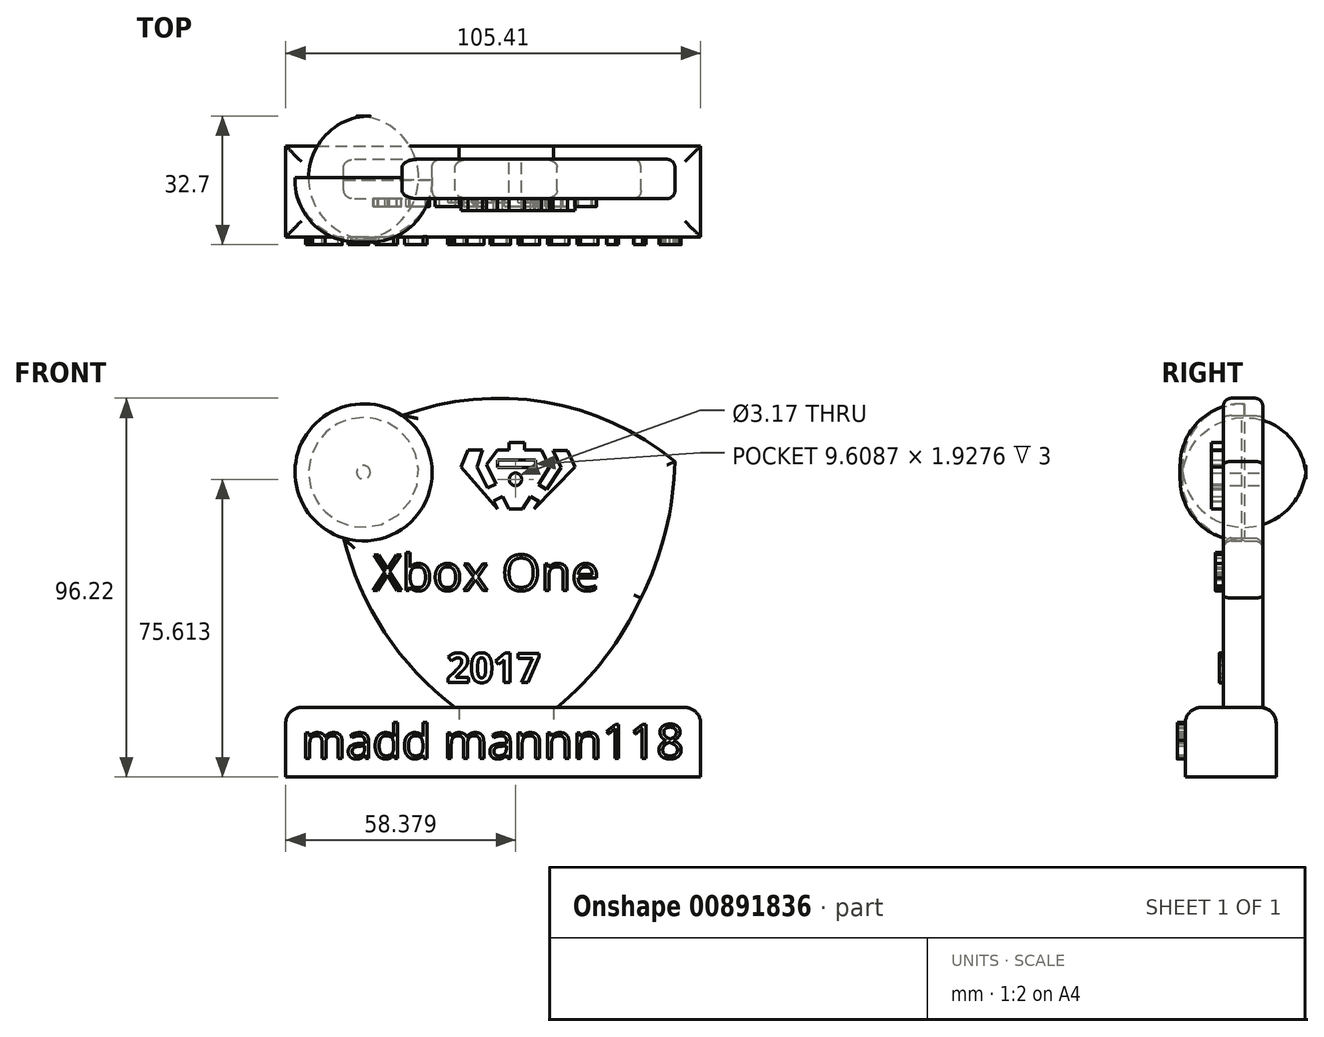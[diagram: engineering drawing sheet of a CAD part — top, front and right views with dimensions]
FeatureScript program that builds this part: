
annotation { "Feature Type Name" : "Feature", "Feature Type Description" : "" }
export const myFeature = defineFeature(function(context is Context, id is Id, definition is map)
    precondition{}
    {
        {
            var Q0;
            Q0=qCreatedBy(makeId("Front.planeOp"),FACE);
            var sketch = newSketch(context, id + "F0", { "sketchPlane" : qUnion([Q0])});
            skArc(sketch, "E0", {"start": v(0, -36.03) * mm, "mid": v(19.7, -20.75) * mm, "end": v(33.53, 0) * mm});
            skArc(sketch, "E1", {"start": v(33.53, 0) * mm, "mid": v(39.77, 16.9) * mm, "end": v(42.15, 34.74) * mm});
            skCircle(sketch, "E2", {"center": v(-36.94, 31.97) * mm, "radius": 17.42 * mm});
            skArc(sketch, "E3", {"start": v(-42.01, 15.3) * mm, "mid": v(-26.81, -15.11) * mm, "end": v(0, -36.03) * mm});
            skPoint(sketch, "E4.end.orphan", {"position": v(0, 41.46) * mm});
            skArc(sketch, "E5", {"start": v(42.15, 34.74) * mm, "mid": v(0.72, 50.74) * mm, "end": v(-42.01, 38.66) * mm});
            skSolve(sketch);
        }
        {
            var Q0;
            {var subQ0=sQuery(id+"F0.wireOp",EDGE,"E2");var subQ1=makeQuery(id+"F0.imprint","INTERSECT",VERTEX,{"derivedFrom":[subQ0,sQuery(id+"F0.wireOp",EDGE,"E3")]});Q0=makeQuery(id+"F0.imprint","IMPRINT",FACE,{"disambiguationData":[TD([[makeQuery(id+"F0.imprint","IMPRINT",EDGE,{"disambiguationData":[TD([[subQ1,1.0]])],"derivedFrom":subQ0}),1.0]])]});}
            extrude(context, id + "F1", {"entities" : qUnion([Q0]), "depth" : 16 * mm, "offsetDistance" : 25 * mm, "hasSecondDirection" : true, "secondDirectionOppositeDirection" : true, "secondDirectionDepth" : 16 * mm});
        }
        {
            var Q0;
            Q0=makeQuery(id+"F1.opExtrude","CAP_EDGE",EDGE,{"disambiguationData":[OSD([sQuery(id+"F0.wireOp",EDGE,"E2")])],"isStart":false});
            var Q1;
            Q1=makeQuery(id+"F1.opExtrude","CAP_EDGE",EDGE,{"disambiguationData":[OSD([sQuery(id+"F0.wireOp",EDGE,"E2")])],"isStart":true});
            fillet(context, id + "F2", {"entities" : qUnion([Q0, Q1]), "radius" : 15.7 * mm, "tangentPropagation" : true, "allowEdgeOverflow" : false});
        }
        {
            var Q0;
            Q0=makeQuery(id+"F0.imprint","IMPRINT",FACE,{"disambiguationData":[TD([[makeQuery(id+"F0.imprint","IMPRINT",EDGE,{"derivedFrom":sQuery(id+"F0.wireOp",EDGE,"E0")}),1.0]])]});
            extrude(context, id + "F3", {"entities" : qUnion([Q0]), "operationType" : NewBodyOperationType.ADD, "depth" : 5 * mm, "offsetDistance" : 25 * mm, "hasSecondDirection" : true, "secondDirectionOppositeDirection" : true, "secondDirectionDepth" : 5 * mm});
        }
        {
            var Q0;
            Q0=makeQuery(id+"F3.opExtrude","CAP_FACE",FACE,{"disambiguationData":[OSD([sQuery(id+"F0.wireOp",EDGE,"E0"),sQuery(id+"F0.wireOp",EDGE,"E1"),sQuery(id+"F0.wireOp",EDGE,"E2"),sQuery(id+"F0.wireOp",EDGE,"E3"),sQuery(id+"F0.wireOp",EDGE,"E5")])],"isStart":false});
            cPlane(context, id + "F4", {"entities" : qUnion([Q0]), "cplaneType" : CPlaneType.OFFSET, "offset" : 0 * mm, "width" : 150 * mm, "height" : 150 * mm});
        }
        {
            var Q0;
            Q0=qCreatedBy(id+"F4.planeOp",FACE);
            var sketch = newSketch(context, id + "F5", { "sketchPlane" : qUnion([Q0])});
            skText(sketch, "E6", { "text": "Rocket league\n", "fontName": "OpenSans-Regular.ttf"});
            const initialGuessF5  = {"E6": [-0.03247, -0.00599, 1, 0, 0.0069]};
            skSetInitialGuess(sketch, initialGuessF5);
            skSolve(sketch);
        }
        {
            var Q0;
            Q0 = qConstructionFilter(qBodyType(qCreatedBy(id + "F5" ,EDGE), BodyType.WIRE), ConstructionObject.NO);
            extrude(context, id + "F6", {"bodyType" : ToolBodyType.SURFACE, "surfaceEntities" : qUnion([Q0]), "depth" : 1 * mm, "offsetDistance" : 25 * mm, "hasSecondDirection" : true, "secondDirectionOppositeDirection" : true, "secondDirectionDepth" : 3 * mm});
        }
        {
            var Q0;
            Q0=makeQuery(id+"F3.opExtrude","CAP_EDGE",EDGE,{"disambiguationData":[OSD([sQuery(id+"F0.wireOp",EDGE,"E2")])],"isStart":false});
            var Q1;
            Q1=makeQuery(id+"F3.opExtrude","CAP_EDGE",EDGE,{"disambiguationData":[OSD([sQuery(id+"F0.wireOp",EDGE,"E3")])],"isStart":false});
            var Q2;
            Q2=makeQuery(id+"F3.opExtrude","CAP_EDGE",EDGE,{"disambiguationData":[OSD([sQuery(id+"F0.wireOp",EDGE,"E0")])],"isStart":false});
            var Q3;
            Q3=makeQuery(id+"F3.opExtrude","CAP_EDGE",EDGE,{"disambiguationData":[OSD([sQuery(id+"F0.wireOp",EDGE,"E1")])],"isStart":false});
            var Q4;
            Q4=makeQuery(id+"F3.opExtrude","CAP_EDGE",EDGE,{"disambiguationData":[OSD([sQuery(id+"F0.wireOp",EDGE,"E5")])],"isStart":false});
            var Q5;
            Q5=makeQuery(id+"F3.opExtrude","CAP_EDGE",EDGE,{"disambiguationData":[OSD([sQuery(id+"F0.wireOp",EDGE,"E2")])],"isStart":true});
            var Q6;
            Q6=makeQuery(id+"F3.opExtrude","CAP_EDGE",EDGE,{"disambiguationData":[OSD([sQuery(id+"F0.wireOp",EDGE,"E3")])],"isStart":true});
            var Q7;
            Q7=makeQuery(id+"F3.opExtrude","CAP_EDGE",EDGE,{"disambiguationData":[OSD([sQuery(id+"F0.wireOp",EDGE,"E0")])],"isStart":true});
            var Q8;
            Q8=makeQuery(id+"F3.opExtrude","CAP_EDGE",EDGE,{"disambiguationData":[OSD([sQuery(id+"F0.wireOp",EDGE,"E1")])],"isStart":true});
            var Q9;
            Q9=makeQuery(id+"F3.opExtrude","CAP_EDGE",EDGE,{"disambiguationData":[OSD([sQuery(id+"F0.wireOp",EDGE,"E5")])],"isStart":true});
            fillet(context, id + "F7", {"entities" : qUnion([Q0, Q1, Q2, Q3, Q4, Q5, Q6, Q7, Q8, Q9]), "radius" : 2 * mm, "tangentPropagation" : true, "allowEdgeOverflow" : false});
        }
        {
            var Q0;
            Q0=qCreatedBy(id+"F4.planeOp",FACE);
            var sketch = newSketch(context, id + "F8", { "sketchPlane" : qUnion([Q0])});
            skLineSegment(sketch, "E7", {"start": v(-2.84, 22.63) * mm, "end": v(-8.12, 33.39) * mm});
            skLineSegment(sketch, "E8", {"start": v(-8.12, 33.39) * mm, "end": v(-6.7, 37.65) * mm});
            skLineSegment(sketch, "E9", {"start": v(-6.7, 37.65) * mm, "end": v(-10.35, 37.65) * mm});
            skLineSegment(sketch, "E10", {"start": v(-10.35, 37.65) * mm, "end": v(-12.18, 33.39) * mm});
            skLineSegment(sketch, "E11", {"start": v(-12.18, 33.39) * mm, "end": v(-2.84, 22.63) * mm});
            skLineSegment(sketch, "E12", {"start": v(0, 22.63) * mm, "end": v(3.45, 22.63) * mm});
            skLineSegment(sketch, "E13", {"start": v(3.45, 22.63) * mm, "end": v(5.48, 25.88) * mm});
            skLineSegment(sketch, "E14", {"start": v(7.49, 28.86) * mm, "end": v(10.32, 33.39) * mm});
            skLineSegment(sketch, "E15", {"start": v(10.32, 33.39) * mm, "end": v(8.23, 37.65) * mm});
            skLineSegment(sketch, "E16", {"start": v(8.23, 37.65) * mm, "end": v(-2.84, 37.65) * mm});
            skLineSegment(sketch, "E17", {"start": v(0, 22.63) * mm, "end": v(-1.6, 25.88) * mm});
            skLineSegment(sketch, "E18", {"start": v(-1.6, 25.88) * mm, "end": v(-3.88, 24.75) * mm});
            skLineSegment(sketch, "E19", {"start": v(-3.88, 24.75) * mm, "end": v(-5.48, 28) * mm});
            skLineSegment(sketch, "E20", {"start": v(-5.48, 28) * mm, "end": v(-3.32, 29.07) * mm});
            skLineSegment(sketch, "E21", {"start": v(-3.32, 29.07) * mm, "end": v(-5.73, 33.97) * mm});
            skLineSegment(sketch, "E22", {"start": v(-5.73, 33.97) * mm, "end": v(-2.84, 37.65) * mm});
            skLineSegment(sketch, "E23", {"start": v(6.33, 22.63) * mm, "end": v(13.22, 33.24) * mm});
            skLineSegment(sketch, "E24", {"start": v(13.22, 33.24) * mm, "end": v(11.15, 37.48) * mm});
            skLineSegment(sketch, "E25", {"start": v(11.15, 37.48) * mm, "end": v(14.84, 37.48) * mm});
            skLineSegment(sketch, "E26", {"start": v(14.84, 37.48) * mm, "end": v(16.85, 33.39) * mm});
            skLineSegment(sketch, "E27", {"start": v(16.85, 33.39) * mm, "end": v(6.33, 22.63) * mm});
            skLineSegment(sketch, "E28", {"start": v(5.48, 25.88) * mm, "end": v(7.98, 24.32) * mm});
            skLineSegment(sketch, "E29", {"start": v(7.49, 28.86) * mm, "end": v(10.55, 26.95) * mm});
            skLineSegment(sketch, "E30", {"start": v(-1.6, 25.88) * mm, "end": v(1.79, 27.54) * mm});
            skLineSegment(sketch, "E31", {"start": v(1.79, 27.54) * mm, "end": v(5.48, 25.88) * mm});
            skLineSegment(sketch, "E32", {"start": v(-3.32, 29.07) * mm, "end": v(0, 30.7) * mm});
            skLineSegment(sketch, "E33", {"start": v(0, 30.7) * mm, "end": v(1.79, 27.54) * mm});
            skLineSegment(sketch, "E34", {"start": v(7.49, 28.86) * mm, "end": v(4, 31.12) * mm});
            skPoint(sketch, "E34.endSnap0", {"position": v(8.9, 31.12) * mm});
            skLineSegment(sketch, "E35", {"start": v(4, 31.12) * mm, "end": v(1.79, 27.54) * mm});
            skLineSegment(sketch, "E36", {"start": v(4, 31.12) * mm, "end": v(4, 39.53) * mm});
            skLineSegment(sketch, "E37", {"start": v(4, 39.53) * mm, "end": v(0, 39.53) * mm});
            skLineSegment(sketch, "E38", {"start": v(0, 39.53) * mm, "end": v(0, 30.7) * mm});
            skLineSegment(sketch, "E39", {"start": v(0, 30.7) * mm, "end": v(4, 31.12) * mm});
            skLineSegment(sketch, "E40", {"start": v(-2.84, 35.11) * mm, "end": v(6.77, 35.11) * mm});
            skPoint(sketch, "E40.startSnap0", {"position": v(0, 35.11) * mm});
            skLineSegment(sketch, "E41", {"start": v(6.77, 35.11) * mm, "end": v(6.77, 33.18) * mm});
            skLineSegment(sketch, "E42", {"start": v(6.77, 33.18) * mm, "end": v(-2.84, 33.18) * mm});
            skLineSegment(sketch, "E43", {"start": v(-2.84, 33.18) * mm, "end": v(-2.84, 35.11) * mm});
            skSolve(sketch);
        }
        {
            var Q0;
            {var subQ0=sQuery(id+"F8.wireOp",EDGE,"E38");var subQ1=sQuery(id+"F8.wireOp",EDGE,"E16");var subQ2=makeQuery(id+"F8.imprint","INTERSECT",VERTEX,{"derivedFrom":[subQ1,subQ0]});var subQ5=makeQuery(id+"F8.imprint","IMPRINT",EDGE,{"disambiguationData":[TD([[subQ2,1.0]])],"derivedFrom":subQ1});var subQ6=sQuery(id+"F8.wireOp",EDGE,"E37");var subQ12=sQuery(id+"F8.wireOp",EDGE,"E29");var subQ13=sQuery(id+"F8.wireOp",EDGE,"E23");var subQ14=makeQuery(id+"F8.imprint","INTERSECT",VERTEX,{"derivedFrom":[subQ13,subQ12]});var subQ15=sQuery(id+"F8.wireOp",EDGE,"E28");var subQ16=makeQuery(id+"F8.imprint","INTERSECT",VERTEX,{"derivedFrom":[subQ13,subQ15]});var subQ17=makeQuery(id+"F8.imprint","IMPRINT",EDGE,{"disambiguationData":[TD([[subQ14,1.0]])],"derivedFrom":subQ13});var subQ23=sQuery(id+"F8.wireOp",EDGE,"E31");var subQ24=makeQuery(id+"F8.imprint","IMPRINT",EDGE,{"derivedFrom":subQ23});var subQ27=sQuery(id+"F8.wireOp",EDGE,"E14");var subQ31=sQuery(id+"F8.wireOp",EDGE,"E8");var subQ32=sQuery(id+"F8.wireOp",EDGE,"E18");var subQ48=sQuery(id+"F8.wireOp",EDGE,"E24");Q0=qUnion([makeQuery(id+"F8.imprint","IMPRINT",FACE,{"disambiguationData":[TD([[makeQuery(id+"F8.imprint","IMPRINT",EDGE,{"derivedFrom":sQuery(id+"F8.wireOp",EDGE,"E21")}),-1.0]])]}),makeQuery(id+"F8.imprint","IMPRINT",FACE,{"disambiguationData":[TD([[makeQuery(id+"F8.imprint","IMPRINT",EDGE,{"derivedFrom":subQ48}),-1.0]])]}),makeQuery(id+"F8.imprint","IMPRINT",FACE,{"disambiguationData":[TD([[makeQuery(id+"F8.imprint","IMPRINT",EDGE,{"derivedFrom":subQ32}),-1.0]])]}),makeQuery(id+"F8.imprint","IMPRINT",FACE,{"disambiguationData":[TD([[makeQuery(id+"F8.imprint","IMPRINT",EDGE,{"disambiguationData":[TD([[subQ16,1.0]])],"derivedFrom":subQ13}),-1.0]])]}),makeQuery(id+"F8.imprint","IMPRINT",FACE,{"disambiguationData":[TD([[makeQuery(id+"F8.imprint","IMPRINT",EDGE,{"derivedFrom":subQ27}),1.0]])]}),makeQuery(id+"F8.imprint","IMPRINT",FACE,{"disambiguationData":[TD([[makeQuery(id+"F8.imprint","IMPRINT",EDGE,{"derivedFrom":subQ31}),1.0]])]}),makeQuery(id+"F8.imprint","IMPRINT",FACE,{"disambiguationData":[TD([[makeQuery(id+"F8.imprint","IMPRINT",EDGE,{"derivedFrom":sQuery(id+"F8.wireOp",EDGE,"E12")}),1.0]])]}),makeQuery(id+"F8.imprint","IMPRINT",FACE,{"disambiguationData":[TD([[subQ24,1.0]])]}),makeQuery(id+"F8.imprint","IMPRINT",FACE,{"disambiguationData":[TD([[subQ17,-1.0]])]}),makeQuery(id+"F8.imprint","IMPRINT",FACE,{"disambiguationData":[TD([[subQ5,1.0]])]}),makeQuery(id+"F8.imprint","IMPRINT",FACE,{"disambiguationData":[TD([[makeQuery(id+"F8.imprint","IMPRINT",EDGE,{"derivedFrom":subQ6}),1.0]])]})]);}
            var Q1;
            Q1=makeQuery(id+"F8.imprint","IMPRINT",FACE,{"disambiguationData":[TD([[makeQuery(id+"F8.imprint","IMPRINT",EDGE,{"derivedFrom":sQuery(id+"F8.wireOp",EDGE,"E33")}),1.0]])]});
            var Q2;
            {var subQ0=sQuery(id+"F8.wireOp",EDGE,"E39");Q2=makeQuery(id+"F8.imprint","IMPRINT",FACE,{"disambiguationData":[TD([[makeQuery(id+"F8.imprint","IMPRINT",EDGE,{"derivedFrom":subQ0}),1.0]])]});}
            extrude(context, id + "F9", {"entities" : qUnion([Q0, Q1, Q2]), "operationType" : NewBodyOperationType.ADD, "depth" : 3 * mm, "offsetDistance" : 25 * mm});
        }
        {
            var Q0;
            Q0=qCreatedBy(id+"F4.planeOp",FACE);
            var sketch = newSketch(context, id + "F10", { "sketchPlane" : qUnion([Q0])});
            skCircle(sketch, "E44", {"center": v(1.67, 30.2) * mm, "radius": 1.58 * mm});
            skSolve(sketch);
        }
        {
            var Q0;
            Q0 = qSketchRegion(id + "F10", true);
            extrude(context, id + "F11", {"entities" : qUnion([Q0]), "operationType" : NewBodyOperationType.REMOVE, "depth" : 47.6 * mm, "offsetDistance" : 25 * mm, "hasSecondDirection" : true, "secondDirectionOppositeDirection" : true, "secondDirectionDepth" : 25 * mm});
        }
        {
            var Q0;
            Q0=qCreatedBy(makeId("Front.planeOp"),FACE);
            var sketch = newSketch(context, id + "F12", { "sketchPlane" : qUnion([Q0])});
            skLineSegment(sketch, "E45.bottom", {"start": v(-56.7, -45.4) * mm, "end": v(48.7, -45.4) * mm});
            skLineSegment(sketch, "E45.top", {"start": v(-56.7, -27.77) * mm, "end": v(48.7, -27.77) * mm});
            skLineSegment(sketch, "E45.left", {"start": v(-56.7, -45.4) * mm, "end": v(-56.7, -27.77) * mm});
            skLineSegment(sketch, "E45.right", {"start": v(48.7, -45.4) * mm, "end": v(48.7, -27.77) * mm});
            skSolve(sketch);
        }
        {
            var Q0;
            Q0 = qSketchRegion(id + "F12", true);
            extrude(context, id + "F13", {"entities" : qUnion([Q0]), "operationType" : NewBodyOperationType.ADD, "depth" : 14.7 * mm, "offsetDistance" : 25 * mm, "hasSecondDirection" : true, "secondDirectionOppositeDirection" : true, "secondDirectionDepth" : 8.4 * mm});
        }
        {
            var Q0;
            Q0=makeQuery(id+"F13.opExtrude","CAP_FACE",FACE,{"disambiguationData":[OSD([sQuery(id+"F12.wireOp",EDGE,"E45.bottom"),sQuery(id+"F12.wireOp",EDGE,"E45.top"),sQuery(id+"F12.wireOp",EDGE,"E45.left"),sQuery(id+"F12.wireOp",EDGE,"E45.right")])],"isStart":false});
            cPlane(context, id + "F14", {"entities" : qUnion([Q0]), "cplaneType" : CPlaneType.OFFSET, "offset" : 0 * mm, "width" : 150 * mm, "height" : 150 * mm});
        }
        {
            var Q0;
            Q0=qCreatedBy(id+"F14.planeOp",FACE);
            var sketch = newSketch(context, id + "F15", { "sketchPlane" : qUnion([Q0])});
            skText(sketch, "E46", { "text": "madd mannn118\n", "fontName": "OpenSans-Regular.ttf"});
            const initialGuessF15  = {"E46": [-0.05266, -0.04074, 1, 0, 0.00872]};
            skSetInitialGuess(sketch, initialGuessF15);
            skSolve(sketch);
        }
        {
            var Q0;
            Q0 = qSketchRegion(id + "F15", true);
            extrude(context, id + "F16", {"entities" : qUnion([Q0]), "operationType" : NewBodyOperationType.ADD, "depth" : 2 * mm, "offsetDistance" : 25 * mm});
        }
        {
            var Q0;
            Q0=qCreatedBy(id+"F4.planeOp",FACE);
            var sketch = newSketch(context, id + "F17", { "sketchPlane" : qUnion([Q0])});
            skText(sketch, "E47", { "text": "Xbox One", "fontName": "OpenSans-Regular.ttf"});
            const initialGuessF17  = {"E47": [-0.03452, 0.00193, 1, 0, 0.00913]};
            skSetInitialGuess(sketch, initialGuessF17);
            skSolve(sketch);
        }
        {
            var Q0;
            Q0 = qSketchRegion(id + "F17", true);
            extrude(context, id + "F18", {"entities" : qUnion([Q0]), "operationType" : NewBodyOperationType.ADD, "depth" : 2 * mm, "offsetDistance" : 25 * mm});
        }
        {
            var Q0;
            Q0=qCreatedBy(id+"F4.planeOp",FACE);
            var sketch = newSketch(context, id + "F19", { "sketchPlane" : qUnion([Q0])});
            skText(sketch, "E48", { "text": "2017", "fontName": "OpenSans-Bold.ttf"});
            const initialGuessF19  = {"E48": [-0.01585, -0.02141, 1, 0, 0.0075]};
            skSetInitialGuess(sketch, initialGuessF19);
            skSolve(sketch);
        }
        {
            var Q0;
            Q0 = qSketchRegion(id + "F19", true);
            extrude(context, id + "F20", {"entities" : qUnion([Q0]), "operationType" : NewBodyOperationType.ADD, "depth" : 1 * mm, "offsetDistance" : 25 * mm});
        }
        {
            var Q0;
            Q0=makeQuery(id+"F13.opExtrude","CAP_EDGE",EDGE,{"disambiguationData":[OSD([sQuery(id+"F12.wireOp",EDGE,"E45.top")])],"isStart":false});
            var Q1;
            Q1=makeQuery(id+"F13.opExtrude","SWEPT_EDGE",EDGE,{"disambiguationData":[OSD([sQuery(id+"F12.wireOp",EDGE,"E45.top"),sQuery(id+"F12.wireOp",EDGE,"E45.left")])]});
            var Q2;
            Q2=makeQuery(id+"F13.opExtrude","SWEPT_EDGE",EDGE,{"disambiguationData":[OSD([sQuery(id+"F12.wireOp",EDGE,"E45.top"),sQuery(id+"F12.wireOp",EDGE,"E45.right")])]});
            var Q3;
            Q3=makeQuery(id+"F13.opExtrude","CAP_EDGE",EDGE,{"disambiguationData":[OSD([sQuery(id+"F12.wireOp",EDGE,"E45.top")])],"isStart":true});
            fillet(context, id + "F21", {"entities" : qUnion([Q0, Q1, Q2, Q3]), "radius" : 4 * mm, "tangentPropagation" : true, "allowEdgeOverflow" : false});
        }
    });
